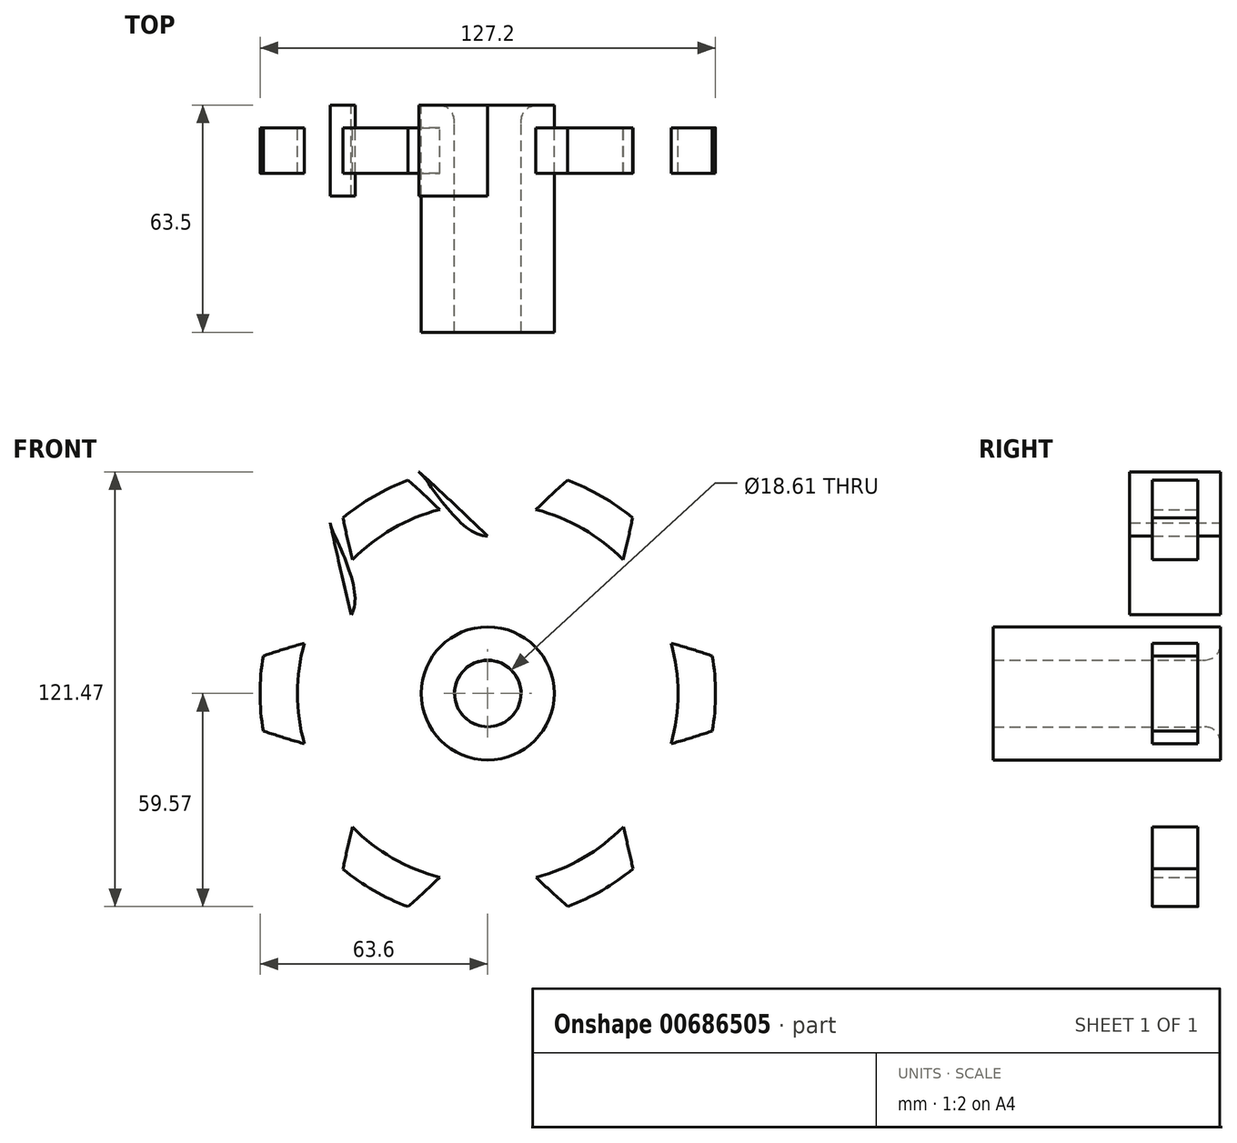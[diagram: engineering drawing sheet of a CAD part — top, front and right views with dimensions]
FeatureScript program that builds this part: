
annotation { "Feature Type Name" : "Feature", "Feature Type Description" : "" }
export const myFeature = defineFeature(function(context is Context, id is Id, definition is map)
    precondition{}
    {
        {
            var Q0;
            Q0=qCreatedBy(makeId("Front.planeOp"),FACE);
            var sketch = newSketch(context, id + "F0", { "sketchPlane" : qUnion([Q0])});
            skPoint(sketch, "E0.0.midPoint", {"position": v(0, -76.2) * mm});
            skFitSpline(sketch, "E1", {"points": [v(-38.1, 22) * mm, v(-44, 76.2) * mm, v(0, 44) * mm], "startDerivative": vector(-36.74, 151.62) * mm, "endDerivative": vector(112.93, -107.62) * mm});
            skFitSpline(sketch, "E2", {"points": [v(0, 44) * mm, v(44, 76.2) * mm, v(38.1, 22) * mm], "startDerivative": vector(112.93, 107.62) * mm, "endDerivative": vector(-36.74, -151.62) * mm});
            skFitSpline(sketch, "E3", {"points": [v(38.1, 22) * mm, v(87.99, 0) * mm, v(38.1, -22) * mm], "startDerivative": vector(149.67, -44) * mm, "endDerivative": vector(-149.67, -44) * mm});
            skFitSpline(sketch, "E4", {"points": [v(38.1, -22) * mm, v(44, -76.2) * mm, v(0, -44) * mm], "startDerivative": vector(36.74, -151.62) * mm, "endDerivative": vector(-112.93, 107.62) * mm});
            skFitSpline(sketch, "E5", {"points": [v(0, -44) * mm, v(-44, -76.2) * mm, v(-38.1, -22) * mm], "startDerivative": vector(-112.93, -107.62) * mm, "endDerivative": vector(36.74, 151.62) * mm});
            skFitSpline(sketch, "E6", {"points": [v(-38.1, -22) * mm, v(-87.99, 0) * mm, v(-38.1, 22) * mm], "startDerivative": vector(-149.67, 44) * mm, "endDerivative": vector(149.67, 44) * mm});
            skFitSpline(sketch, "E7", {"points": [v(-63.04, 14.66) * mm, v(-38.1, 22) * mm, v(-44.22, 47.27) * mm], "startDerivative": vector(65.42, 5.7) * mm, "endDerivative": vector(-27.78, 59.5) * mm});
            skFitSpline(sketch, "E8", {"points": [v(-18.82, 61.93) * mm, v(0, 44) * mm, v(18.82, 61.93) * mm], "startDerivative": vector(37.64, -53.81) * mm, "endDerivative": vector(37.64, 53.81) * mm});
            skFitSpline(sketch, "E9", {"points": [v(44.22, 47.27) * mm, v(38.1, 22) * mm, v(63.04, 14.66) * mm], "startDerivative": vector(-27.78, -59.5) * mm, "endDerivative": vector(65.42, -5.7) * mm});
            skFitSpline(sketch, "E10", {"points": [v(63.04, -14.66) * mm, v(38.1, -22) * mm, v(44.22, -47.27) * mm], "startDerivative": vector(-65.42, -5.7) * mm, "endDerivative": vector(27.78, -59.5) * mm});
            skFitSpline(sketch, "E11", {"points": [v(18.82, -61.93) * mm, v(0, -44) * mm, v(-18.82, -61.93) * mm], "startDerivative": vector(-37.64, 53.81) * mm, "endDerivative": vector(-37.64, -53.81) * mm});
            skFitSpline(sketch, "E12", {"points": [v(-44.22, -47.27) * mm, v(-38.1, -22) * mm, v(-63.04, -14.66) * mm], "startDerivative": vector(27.78, 59.5) * mm, "endDerivative": vector(-65.42, 5.7) * mm});
            skPoint(sketch, "E13.visualSharp", {"position": v(61.79, 14.77) * mm});
            skArc(sketch, "E13.filletArc", {"start": v(63.22, 14.3) * mm, "mid": v(61.8, 14.68) * mm, "end": v(60.33, 14.9) * mm});
            skPoint(sketch, "E14.visualSharp", {"position": v(61.79, -14.77) * mm});
            skArc(sketch, "E14.filletArc", {"start": v(60.33, -14.9) * mm, "mid": v(61.8, -14.68) * mm, "end": v(63.22, -14.3) * mm});
            skPoint(sketch, "E15.visualSharp", {"position": v(43.69, -46.12) * mm});
            skArc(sketch, "E15.filletArc", {"start": v(44, -47.6) * mm, "mid": v(43.61, -46.17) * mm, "end": v(43.07, -44.8) * mm});
            skPoint(sketch, "E16.visualSharp", {"position": v(18.1, -60.9) * mm});
            skArc(sketch, "E16.filletArc", {"start": v(17.26, -59.7) * mm, "mid": v(18.18, -60.86) * mm, "end": v(19.23, -61.9) * mm});
            skPoint(sketch, "E17.visualSharp", {"position": v(-18.1, -60.9) * mm});
            skArc(sketch, "E17.filletArc", {"start": v(-19.23, -61.9) * mm, "mid": v(-18.18, -60.86) * mm, "end": v(-17.26, -59.7) * mm});
            skPoint(sketch, "E18.visualSharp", {"position": v(-43.69, -46.12) * mm});
            skArc(sketch, "E18.filletArc", {"start": v(-43.07, -44.8) * mm, "mid": v(-43.61, -46.17) * mm, "end": v(-44, -47.6) * mm});
            skPoint(sketch, "E19.visualSharp", {"position": v(-61.79, -14.77) * mm});
            skArc(sketch, "E19.filletArc", {"start": v(-63.22, -14.3) * mm, "mid": v(-61.8, -14.68) * mm, "end": v(-60.33, -14.9) * mm});
            skPoint(sketch, "E20.visualSharp", {"position": v(-61.79, 14.77) * mm});
            skArc(sketch, "E20.filletArc", {"start": v(-60.33, 14.9) * mm, "mid": v(-61.8, 14.68) * mm, "end": v(-63.22, 14.3) * mm});
            skPoint(sketch, "E21.visualSharp", {"position": v(-43.69, 46.12) * mm});
            skArc(sketch, "E21.filletArc", {"start": v(-44, 47.6) * mm, "mid": v(-43.61, 46.17) * mm, "end": v(-43.07, 44.8) * mm});
            skPoint(sketch, "E22.visualSharp", {"position": v(-18.1, 60.9) * mm});
            skArc(sketch, "E22.filletArc", {"start": v(-17.26, 59.7) * mm, "mid": v(-18.18, 60.86) * mm, "end": v(-19.23, 61.9) * mm});
            skPoint(sketch, "E23.visualSharp", {"position": v(18.1, 60.9) * mm});
            skArc(sketch, "E23.filletArc", {"start": v(19.23, 61.9) * mm, "mid": v(18.18, 60.86) * mm, "end": v(17.26, 59.7) * mm});
            skPoint(sketch, "E24.visualSharp", {"position": v(43.69, 46.12) * mm});
            skArc(sketch, "E24.filletArc", {"start": v(43.07, 44.8) * mm, "mid": v(43.61, 46.17) * mm, "end": v(44, 47.6) * mm});
            skCircle(sketch, "E25", {"center": v(0, 0) * mm, "radius": 9.3 * mm});
            skArc(sketch, "E26", {"start": v(-35.36, 14.2) * mm, "mid": v(-38.1, 0) * mm, "end": v(-35.36, -14.2) * mm});
            skCircle(sketch, "E27.cCircle", {"center": v(0, 0) * mm, "radius": 9.3 * mm, "construction": true});
            skPoint(sketch, "E27.0.midPoint", {"position": v(0, 9.3) * mm});
            skLineSegment(sketch, "E28", {"start": v(-18.1, 4.25) * mm, "end": v(-35.36, 14.2) * mm});
            skLineSegment(sketch, "E29", {"start": v(-12.73, 13.55) * mm, "end": v(-29.98, 23.51) * mm});
            skLineSegment(sketch, "E30", {"start": v(-5.37, 17.8) * mm, "end": v(-5.37, 37.72) * mm});
            skLineSegment(sketch, "E31", {"start": v(5.37, 17.8) * mm, "end": v(5.37, 37.72) * mm});
            skLineSegment(sketch, "E32", {"start": v(12.73, 13.55) * mm, "end": v(29.98, 23.51) * mm});
            skLineSegment(sketch, "E33", {"start": v(18.1, 4.25) * mm, "end": v(35.36, 14.2) * mm});
            skLineSegment(sketch, "E34", {"start": v(18.1, -4.25) * mm, "end": v(35.36, -14.2) * mm});
            skLineSegment(sketch, "E35", {"start": v(12.73, -13.55) * mm, "end": v(29.98, -23.51) * mm});
            skLineSegment(sketch, "E36", {"start": v(5.37, -17.8) * mm, "end": v(5.37, -37.72) * mm});
            skLineSegment(sketch, "E37", {"start": v(-5.37, -17.8) * mm, "end": v(-5.37, -37.72) * mm});
            skLineSegment(sketch, "E38", {"start": v(-18.1, -4.25) * mm, "end": v(-35.36, -14.2) * mm});
            skLineSegment(sketch, "E39", {"start": v(-12.73, -13.55) * mm, "end": v(-29.98, -23.51) * mm});
            skPoint(sketch, "E40.orphan", {"position": v(5.37, 9.3) * mm});
            skPoint(sketch, "E27.0.start.orphan", {"position": v(-5.37, 9.3) * mm});
            skArc(sketch, "E41.trimOffspring", {"start": v(-5.37, 17.8) * mm, "mid": v(-9.3, 16.1) * mm, "end": v(-12.73, 13.55) * mm});
            skArc(sketch, "E42.trimOffspring", {"start": v(12.73, 13.55) * mm, "mid": v(9.3, 16.1) * mm, "end": v(5.37, 17.8) * mm});
            skArc(sketch, "E43.trimOffspring", {"start": v(18.1, -4.25) * mm, "mid": v(18.6, 0) * mm, "end": v(18.1, 4.25) * mm});
            skArc(sketch, "E44.trimOffspring", {"start": v(-5.37, 37.72) * mm, "mid": v(-19.05, 33) * mm, "end": v(-29.98, 23.51) * mm});
            skArc(sketch, "E45.trimOffspring", {"start": v(29.98, 23.51) * mm, "mid": v(19.05, 33) * mm, "end": v(5.37, 37.72) * mm});
            skArc(sketch, "E46.trimOffspring", {"start": v(35.36, -14.2) * mm, "mid": v(38.1, 0) * mm, "end": v(35.36, 14.2) * mm});
            skArc(sketch, "E47.trimOffspring", {"start": v(5.37, -37.72) * mm, "mid": v(19.05, -33) * mm, "end": v(29.98, -23.51) * mm});
            skArc(sketch, "E48.trimOffspring", {"start": v(-29.98, -23.51) * mm, "mid": v(-19.05, -33) * mm, "end": v(-5.37, -37.72) * mm});
            skArc(sketch, "E49", {"start": v(5.37, -17.8) * mm, "mid": v(9.3, -16.1) * mm, "end": v(12.73, -13.55) * mm});
            skArc(sketch, "E50.trimOffspring", {"start": v(-12.73, -13.55) * mm, "mid": v(-9.3, -16.1) * mm, "end": v(-5.37, -17.8) * mm});
            skArc(sketch, "E51.trimOffspring", {"start": v(-18.1, 4.25) * mm, "mid": v(-18.6, 0) * mm, "end": v(-18.1, -4.25) * mm});
            skCircle(sketch, "E52", {"center": v(0, 0) * mm, "radius": 18.6 * mm});
            skArc(sketch, "E53", {"start": v(-40.5, 17.18) * mm, "mid": v(-44, 0) * mm, "end": v(-40.5, -17.18) * mm});
            skFitSpline(sketch, "E54", {"points": [v(-35.13, 26.48) * mm, v(-40.28, 69.77) * mm, v(-5.37, 43.66) * mm], "startDerivative": vector(-30.33, 121.26) * mm, "endDerivative": vector(89.85, -86.9) * mm});
            skFitSpline(sketch, "E55", {"points": [v(5.37, 43.66) * mm, v(40.28, 69.77) * mm, v(35.13, 26.48) * mm], "startDerivative": vector(89.85, 86.9) * mm, "endDerivative": vector(-30.33, -121.26) * mm});
            skFitSpline(sketch, "E56", {"points": [v(40.5, 17.18) * mm, v(80.56, 0) * mm, v(40.5, -17.18) * mm], "startDerivative": vector(120.18, -34.36) * mm, "endDerivative": vector(-120.18, -34.36) * mm});
            skPoint(sketch, "E57.1.internal.snap0", {"position": v(40.28, -69.77) * mm});
            skFitSpline(sketch, "E57", {"points": [v(35.13, -26.48) * mm, v(40.5, -69.77) * mm, v(5.37, -43.66) * mm], "startDerivative": vector(30.97, -121.31) * mm, "endDerivative": vector(-90.45, 86.9) * mm});
            skFitSpline(sketch, "E58", {"points": [v(-5.37, -43.66) * mm, v(-40.28, -69.77) * mm, v(-35.13, -26.48) * mm], "startDerivative": vector(-89.85, -86.9) * mm, "endDerivative": vector(30.33, 121.26) * mm});
            skFitSpline(sketch, "E59", {"points": [v(-40.5, -17.18) * mm, v(-80.56, 0) * mm, v(-40.5, 17.18) * mm], "startDerivative": vector(-120.18, 34.36) * mm, "endDerivative": vector(120.18, 34.36) * mm});
            skArc(sketch, "E60.trimOffspring", {"start": v(-35.13, -26.48) * mm, "mid": v(-22, -38.1) * mm, "end": v(-5.37, -43.66) * mm});
            skArc(sketch, "E61.trimOffspring", {"start": v(5.37, -43.66) * mm, "mid": v(22, -38.1) * mm, "end": v(35.13, -26.48) * mm});
            skArc(sketch, "E62.trimOffspring", {"start": v(40.5, -17.18) * mm, "mid": v(44, 0) * mm, "end": v(40.5, 17.18) * mm});
            skArc(sketch, "E63.trimOffspring", {"start": v(-5.37, 43.66) * mm, "mid": v(-22, 38.1) * mm, "end": v(-35.13, 26.48) * mm});
            skArc(sketch, "E64.trimOffspring", {"start": v(35.13, 26.48) * mm, "mid": v(22, 38.1) * mm, "end": v(5.37, 43.66) * mm});
            skArc(sketch, "E65", {"start": v(-62.73, 10.49) * mm, "mid": v(-63.6, 0) * mm, "end": v(-62.73, -10.49) * mm});
            skArc(sketch, "E66", {"start": v(-51.24, 14.08) * mm, "mid": v(-53.14, 0) * mm, "end": v(-51.24, -14.08) * mm});
            skArc(sketch, "E67.trimOffspring", {"start": v(-22.28, 59.57) * mm, "mid": v(-31.8, 55.08) * mm, "end": v(-40.44, 49.08) * mm});
            skArc(sketch, "E68.trimOffspring", {"start": v(-13.43, 51.41) * mm, "mid": v(-26.57, 46.02) * mm, "end": v(-37.8, 37.34) * mm});
            skArc(sketch, "E69.trimOffspring", {"start": v(40.44, 49.08) * mm, "mid": v(31.8, 55.08) * mm, "end": v(22.28, 59.57) * mm});
            skArc(sketch, "E70.trimOffspring", {"start": v(37.8, 37.34) * mm, "mid": v(26.57, 46.02) * mm, "end": v(13.43, 51.41) * mm});
            skArc(sketch, "E71.trimOffspring", {"start": v(62.73, -10.49) * mm, "mid": v(63.6, 0) * mm, "end": v(62.73, 10.49) * mm});
            skArc(sketch, "E72.trimOffspring", {"start": v(51.24, -14.08) * mm, "mid": v(53.14, 0) * mm, "end": v(51.24, 14.08) * mm});
            skArc(sketch, "E73.trimOffspring", {"start": v(22.36, -59.54) * mm, "mid": v(31.9, -55.02) * mm, "end": v(40.54, -49) * mm});
            skArc(sketch, "E74.trimOffspring", {"start": v(13.47, -51.4) * mm, "mid": v(26.61, -46) * mm, "end": v(37.85, -37.3) * mm});
            skArc(sketch, "E75.trimOffspring", {"start": v(-40.44, -49.08) * mm, "mid": v(-31.8, -55.08) * mm, "end": v(-22.28, -59.57) * mm});
            skArc(sketch, "E76.trimOffspring", {"start": v(-37.8, -37.34) * mm, "mid": v(-26.57, -46.02) * mm, "end": v(-13.43, -51.41) * mm});
            skSolve(sketch);
        }
        {
            var Q0;
            Q0=makeQuery(id+"F0.imprint","IMPRINT",FACE,{"disambiguationData":[TD([[makeQuery(id+"F0.imprint","IMPRINT",EDGE,{"derivedFrom":sQuery(id+"F0.wireOp",EDGE,"E1")}),-1.0]])]});
            extrude(context, id + "F1", {"entities" : qUnion([Q0]), "depth" : 12.7 * mm, "offsetDistance" : 25.4 * mm, "hasSecondDirection" : true, "secondDirectionOppositeDirection" : true, "secondDirectionDepth" : 12.7 * mm});
        }
        {
            var Q0;
            Q0=makeQuery(id+"F0.imprint","IMPRINT",FACE,{"disambiguationData":[TD([[makeQuery(id+"F0.imprint","IMPRINT",EDGE,{"derivedFrom":sQuery(id+"F0.wireOp",EDGE,"E25")}),-1.0]])]});
            extrude(context, id + "F2", {"entities" : qUnion([Q0]), "operationType" : NewBodyOperationType.ADD, "depth" : 50.8 * mm, "offsetDistance" : 25.4 * mm, "hasSecondDirection" : true, "secondDirectionOppositeDirection" : true, "secondDirectionDepth" : 12.7 * mm});
        }
        {
            var Q0;
            {var subQ0=sQuery(id+"F0.wireOp",EDGE,"E67.trimOffspring");Q0=makeQuery(id+"F0.imprint","IMPRINT",FACE,{"disambiguationData":[TD([[makeQuery(id+"F0.imprint","IMPRINT",EDGE,{"derivedFrom":subQ0}),1.0]])]});}
            var Q1;
            {var subQ0=sQuery(id+"F0.wireOp",EDGE,"E69.trimOffspring");Q1=makeQuery(id+"F0.imprint","IMPRINT",FACE,{"disambiguationData":[TD([[makeQuery(id+"F0.imprint","IMPRINT",EDGE,{"derivedFrom":subQ0}),1.0]])]});}
            var Q2;
            {var subQ0=sQuery(id+"F0.wireOp",EDGE,"E73.trimOffspring");Q2=makeQuery(id+"F0.imprint","IMPRINT",FACE,{"disambiguationData":[TD([[makeQuery(id+"F0.imprint","IMPRINT",EDGE,{"derivedFrom":subQ0}),1.0]])]});}
            var Q3;
            {var subQ0=sQuery(id+"F0.wireOp",EDGE,"E71.trimOffspring");Q3=makeQuery(id+"F0.imprint","IMPRINT",FACE,{"disambiguationData":[TD([[makeQuery(id+"F0.imprint","IMPRINT",EDGE,{"derivedFrom":subQ0}),1.0]])]});}
            var Q4;
            {var subQ0=sQuery(id+"F0.wireOp",EDGE,"E75.trimOffspring");Q4=makeQuery(id+"F0.imprint","IMPRINT",FACE,{"disambiguationData":[TD([[makeQuery(id+"F0.imprint","IMPRINT",EDGE,{"derivedFrom":subQ0}),1.0]])]});}
            var Q5;
            {var subQ0=sQuery(id+"F0.wireOp",EDGE,"E65");Q5=makeQuery(id+"F0.imprint","IMPRINT",FACE,{"disambiguationData":[TD([[makeQuery(id+"F0.imprint","IMPRINT",EDGE,{"derivedFrom":subQ0}),1.0]])]});}
            extrude(context, id + "F3", {"entities" : qUnion([Q0, Q1, Q2, Q3, Q4, Q5]), "operationType" : NewBodyOperationType.ADD, "depth" : 6.35 * mm, "offsetDistance" : 25.4 * mm, "hasSecondDirection" : true, "secondDirectionOppositeDirection" : true, "secondDirectionDepth" : 6.35 * mm});
        }
        {
            var Q0;
            Q0=makeQuery(id+"F1.opExtrude","SWEPT_EDGE",EDGE,{"disambiguationData":[OSD([sQuery(id+"F0.wireOp",EDGE,"E29"),sQuery(id+"F0.wireOp",EDGE,"E44.trimOffspring")])]});
            var Q1;
            Q1=makeQuery(id+"F1.opExtrude","SWEPT_EDGE",EDGE,{"disambiguationData":[OSD([sQuery(id+"F0.wireOp",EDGE,"E30"),sQuery(id+"F0.wireOp",EDGE,"E44.trimOffspring")])]});
            var Q2;
            Q2=makeQuery(id+"F1.opExtrude","SWEPT_EDGE",EDGE,{"disambiguationData":[OSD([sQuery(id+"F0.wireOp",EDGE,"E30"),sQuery(id+"F0.wireOp",EDGE,"E52")])]});
            var Q3;
            Q3=makeQuery(id+"F1.opExtrude","SWEPT_EDGE",EDGE,{"disambiguationData":[OSD([sQuery(id+"F0.wireOp",EDGE,"E29"),sQuery(id+"F0.wireOp",EDGE,"E52")])]});
            var Q4;
            Q4=makeQuery(id+"F1.opExtrude","SWEPT_EDGE",EDGE,{"disambiguationData":[OSD([sQuery(id+"F0.wireOp",EDGE,"E31"),sQuery(id+"F0.wireOp",EDGE,"E52")])]});
            var Q5;
            Q5=makeQuery(id+"F1.opExtrude","SWEPT_EDGE",EDGE,{"disambiguationData":[OSD([sQuery(id+"F0.wireOp",EDGE,"E32"),sQuery(id+"F0.wireOp",EDGE,"E52")])]});
            var Q6;
            Q6=makeQuery(id+"F1.opExtrude","SWEPT_EDGE",EDGE,{"disambiguationData":[OSD([sQuery(id+"F0.wireOp",EDGE,"E31"),sQuery(id+"F0.wireOp",EDGE,"E45.trimOffspring")])]});
            var Q7;
            Q7=makeQuery(id+"F1.opExtrude","SWEPT_EDGE",EDGE,{"disambiguationData":[OSD([sQuery(id+"F0.wireOp",EDGE,"E32"),sQuery(id+"F0.wireOp",EDGE,"E45.trimOffspring")])]});
            var Q8;
            Q8=makeQuery(id+"F1.opExtrude","SWEPT_EDGE",EDGE,{"disambiguationData":[OSD([sQuery(id+"F0.wireOp",EDGE,"E33"),sQuery(id+"F0.wireOp",EDGE,"E46.trimOffspring")])]});
            var Q9;
            Q9=makeQuery(id+"F1.opExtrude","SWEPT_EDGE",EDGE,{"disambiguationData":[OSD([sQuery(id+"F0.wireOp",EDGE,"E34"),sQuery(id+"F0.wireOp",EDGE,"E46.trimOffspring")])]});
            var Q10;
            Q10=makeQuery(id+"F1.opExtrude","SWEPT_EDGE",EDGE,{"disambiguationData":[OSD([sQuery(id+"F0.wireOp",EDGE,"E35"),sQuery(id+"F0.wireOp",EDGE,"E47.trimOffspring")])]});
            var Q11;
            Q11=makeQuery(id+"F1.opExtrude","SWEPT_EDGE",EDGE,{"disambiguationData":[OSD([sQuery(id+"F0.wireOp",EDGE,"E36"),sQuery(id+"F0.wireOp",EDGE,"E47.trimOffspring")])]});
            var Q12;
            Q12=makeQuery(id+"F1.opExtrude","SWEPT_EDGE",EDGE,{"disambiguationData":[OSD([sQuery(id+"F0.wireOp",EDGE,"E33"),sQuery(id+"F0.wireOp",EDGE,"E52")])]});
            var Q13;
            Q13=makeQuery(id+"F1.opExtrude","SWEPT_EDGE",EDGE,{"disambiguationData":[OSD([sQuery(id+"F0.wireOp",EDGE,"E34"),sQuery(id+"F0.wireOp",EDGE,"E52")])]});
            var Q14;
            Q14=makeQuery(id+"F1.opExtrude","SWEPT_EDGE",EDGE,{"disambiguationData":[OSD([sQuery(id+"F0.wireOp",EDGE,"E36"),sQuery(id+"F0.wireOp",EDGE,"E52")])]});
            var Q15;
            Q15=makeQuery(id+"F1.opExtrude","SWEPT_EDGE",EDGE,{"disambiguationData":[OSD([sQuery(id+"F0.wireOp",EDGE,"E35"),sQuery(id+"F0.wireOp",EDGE,"E52")])]});
            var Q16;
            Q16=makeQuery(id+"F1.opExtrude","SWEPT_EDGE",EDGE,{"disambiguationData":[OSD([sQuery(id+"F0.wireOp",EDGE,"E37"),sQuery(id+"F0.wireOp",EDGE,"E52")])]});
            var Q17;
            Q17=makeQuery(id+"F1.opExtrude","SWEPT_EDGE",EDGE,{"disambiguationData":[OSD([sQuery(id+"F0.wireOp",EDGE,"E39"),sQuery(id+"F0.wireOp",EDGE,"E52")])]});
            var Q18;
            Q18=makeQuery(id+"F1.opExtrude","SWEPT_EDGE",EDGE,{"disambiguationData":[OSD([sQuery(id+"F0.wireOp",EDGE,"E39"),sQuery(id+"F0.wireOp",EDGE,"E48.trimOffspring")])]});
            var Q19;
            Q19=makeQuery(id+"F1.opExtrude","SWEPT_EDGE",EDGE,{"disambiguationData":[OSD([sQuery(id+"F0.wireOp",EDGE,"E37"),sQuery(id+"F0.wireOp",EDGE,"E48.trimOffspring")])]});
            var Q20;
            Q20=makeQuery(id+"F1.opExtrude","SWEPT_EDGE",EDGE,{"disambiguationData":[OSD([sQuery(id+"F0.wireOp",EDGE,"E26"),sQuery(id+"F0.wireOp",EDGE,"E28")])]});
            var Q21;
            Q21=makeQuery(id+"F1.opExtrude","SWEPT_EDGE",EDGE,{"disambiguationData":[OSD([sQuery(id+"F0.wireOp",EDGE,"E26"),sQuery(id+"F0.wireOp",EDGE,"E38")])]});
            var Q22;
            Q22=makeQuery(id+"F1.opExtrude","SWEPT_EDGE",EDGE,{"disambiguationData":[OSD([sQuery(id+"F0.wireOp",EDGE,"E38"),sQuery(id+"F0.wireOp",EDGE,"E52")])]});
            var Q23;
            Q23=makeQuery(id+"F1.opExtrude","SWEPT_EDGE",EDGE,{"disambiguationData":[OSD([sQuery(id+"F0.wireOp",EDGE,"E28"),sQuery(id+"F0.wireOp",EDGE,"E52")])]});
            var Q24;
            {var subQ0=sQuery(id+"F0.wireOp",EDGE,"E63.trimOffspring");var subQ1=sQuery(id+"F0.wireOp",EDGE,"E54");Q24=makeQuery(id+"F1.opExtrude","SWEPT_EDGE",EDGE,{"disambiguationData":[OSD([subQ1,subQ0]),TDD([makeQuery(id+"F0.imprint","INTERSECT",VERTEX,{"disambiguationData":[OD(0.0)],"derivedFrom":[subQ1,subQ0]})])]});}
            var Q25;
            {var subQ0=sQuery(id+"F0.wireOp",EDGE,"E63.trimOffspring");var subQ1=sQuery(id+"F0.wireOp",EDGE,"E54");Q25=makeQuery(id+"F1.opExtrude","SWEPT_EDGE",EDGE,{"disambiguationData":[OSD([subQ1,subQ0]),TDD([makeQuery(id+"F0.imprint","INTERSECT",VERTEX,{"disambiguationData":[OD(1.0)],"derivedFrom":[subQ1,subQ0]})])]});}
            var Q26;
            {var subQ0=sQuery(id+"F0.wireOp",EDGE,"E64.trimOffspring");var subQ1=sQuery(id+"F0.wireOp",EDGE,"E55");Q26=makeQuery(id+"F1.opExtrude","SWEPT_EDGE",EDGE,{"disambiguationData":[OSD([subQ1,subQ0]),TDD([makeQuery(id+"F0.imprint","INTERSECT",VERTEX,{"disambiguationData":[OD(0.0)],"derivedFrom":[subQ1,subQ0]})])]});}
            var Q27;
            {var subQ0=sQuery(id+"F0.wireOp",EDGE,"E64.trimOffspring");var subQ1=sQuery(id+"F0.wireOp",EDGE,"E55");Q27=makeQuery(id+"F1.opExtrude","SWEPT_EDGE",EDGE,{"disambiguationData":[OSD([subQ1,subQ0]),TDD([makeQuery(id+"F0.imprint","INTERSECT",VERTEX,{"disambiguationData":[OD(1.0)],"derivedFrom":[subQ1,subQ0]})])]});}
            var Q28;
            {var subQ0=sQuery(id+"F0.wireOp",EDGE,"E62.trimOffspring");var subQ1=sQuery(id+"F0.wireOp",EDGE,"E56");Q28=makeQuery(id+"F1.opExtrude","SWEPT_EDGE",EDGE,{"disambiguationData":[OSD([subQ1,subQ0]),TDD([makeQuery(id+"F0.imprint","INTERSECT",VERTEX,{"disambiguationData":[OD(1.0)],"derivedFrom":[subQ1,subQ0]})])]});}
            var Q29;
            {var subQ0=sQuery(id+"F0.wireOp",EDGE,"E62.trimOffspring");var subQ1=sQuery(id+"F0.wireOp",EDGE,"E56");Q29=makeQuery(id+"F1.opExtrude","SWEPT_EDGE",EDGE,{"disambiguationData":[OSD([subQ1,subQ0]),TDD([makeQuery(id+"F0.imprint","INTERSECT",VERTEX,{"disambiguationData":[OD(0.0)],"derivedFrom":[subQ1,subQ0]})])]});}
            var Q30;
            {var subQ0=sQuery(id+"F0.wireOp",EDGE,"E61.trimOffspring");var subQ1=sQuery(id+"F0.wireOp",EDGE,"E57");Q30=makeQuery(id+"F1.opExtrude","SWEPT_EDGE",EDGE,{"disambiguationData":[OSD([subQ1,subQ0]),TDD([makeQuery(id+"F0.imprint","INTERSECT",VERTEX,{"disambiguationData":[OD(0.0)],"derivedFrom":[subQ1,subQ0]})])]});}
            var Q31;
            {var subQ0=sQuery(id+"F0.wireOp",EDGE,"E61.trimOffspring");var subQ1=sQuery(id+"F0.wireOp",EDGE,"E57");Q31=makeQuery(id+"F1.opExtrude","SWEPT_EDGE",EDGE,{"disambiguationData":[OSD([subQ1,subQ0]),TDD([makeQuery(id+"F0.imprint","INTERSECT",VERTEX,{"disambiguationData":[OD(1.0)],"derivedFrom":[subQ1,subQ0]})])]});}
            var Q32;
            {var subQ0=sQuery(id+"F0.wireOp",EDGE,"E60.trimOffspring");var subQ1=sQuery(id+"F0.wireOp",EDGE,"E58");Q32=makeQuery(id+"F1.opExtrude","SWEPT_EDGE",EDGE,{"disambiguationData":[OSD([subQ1,subQ0]),TDD([makeQuery(id+"F0.imprint","INTERSECT",VERTEX,{"disambiguationData":[OD(0.0)],"derivedFrom":[subQ1,subQ0]})])]});}
            var Q33;
            {var subQ0=sQuery(id+"F0.wireOp",EDGE,"E60.trimOffspring");var subQ1=sQuery(id+"F0.wireOp",EDGE,"E58");Q33=makeQuery(id+"F1.opExtrude","SWEPT_EDGE",EDGE,{"disambiguationData":[OSD([subQ1,subQ0]),TDD([makeQuery(id+"F0.imprint","INTERSECT",VERTEX,{"disambiguationData":[OD(1.0)],"derivedFrom":[subQ1,subQ0]})])]});}
            var Q34;
            {var subQ0=sQuery(id+"F0.wireOp",EDGE,"E59");var subQ1=sQuery(id+"F0.wireOp",EDGE,"E53");Q34=makeQuery(id+"F1.opExtrude","SWEPT_EDGE",EDGE,{"disambiguationData":[OSD([subQ1,subQ0]),TDD([makeQuery(id+"F0.imprint","INTERSECT",VERTEX,{"disambiguationData":[OD(1.0)],"derivedFrom":[subQ1,subQ0]})])]});}
            var Q35;
            {var subQ0=sQuery(id+"F0.wireOp",EDGE,"E59");var subQ1=sQuery(id+"F0.wireOp",EDGE,"E53");Q35=makeQuery(id+"F1.opExtrude","SWEPT_EDGE",EDGE,{"disambiguationData":[OSD([subQ1,subQ0]),TDD([makeQuery(id+"F0.imprint","INTERSECT",VERTEX,{"disambiguationData":[OD(0.0)],"derivedFrom":[subQ1,subQ0]})])]});}
            var Q36;
            Q36=makeQuery(id+"F2.opExtrude","CAP_EDGE",EDGE,{"disambiguationData":[OSD([sQuery(id+"F0.wireOp",EDGE,"E25")])],"isStart":true});
            fillet(context, id + "F4", {"entities" : qUnion([Q0, Q1, Q2, Q3, Q4, Q5, Q6, Q7, Q8, Q9, Q10, Q11, Q12, Q13, Q14, Q15, Q16, Q17, Q18, Q19, Q20, Q21, Q22, Q23, Q24, Q25, Q26, Q27, Q28, Q29, Q30, Q31, Q32, Q33, Q34, Q35, Q36]), "radius" : 5.08 * mm, "tangentPropagation" : true, "rho" : 0.5, "crossSection" : FilletCrossSection.CONIC, "allowEdgeOverflow" : false});
        }
    });
